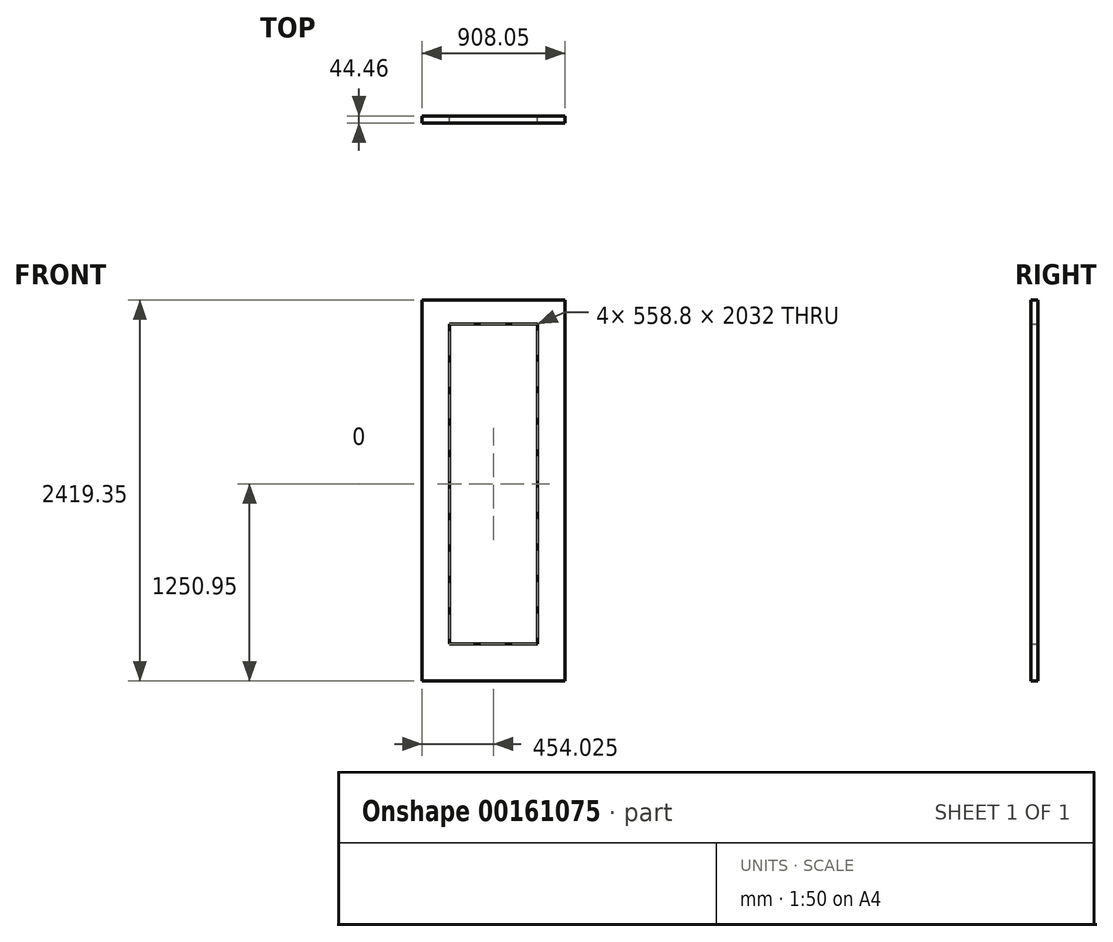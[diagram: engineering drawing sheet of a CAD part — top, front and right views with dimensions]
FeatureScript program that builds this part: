
annotation { "Feature Type Name" : "Feature", "Feature Type Description" : "" }
export const myFeature = defineFeature(function(context is Context, id is Id, definition is map)
    precondition{}
    {
        {
            var Q0;
            Q0=qCreatedBy(makeId("Front.planeOp"),FACE);
            var sketch = newSketch(context, id + "F0", { "sketchPlane" : qUnion([Q0])});
            skLineSegment(sketch, "E0.bottom", {"start": v(0, 0) * mm, "end": v(908.05, 0) * mm});
            skLineSegment(sketch, "E0.top", {"start": v(0, 2419.35) * mm, "end": v(908.05, 2419.35) * mm});
            skLineSegment(sketch, "E0.left", {"start": v(0, 0) * mm, "end": v(0, 2419.35) * mm});
            skLineSegment(sketch, "E0.right", {"start": v(908.05, 0) * mm, "end": v(908.05, 2419.35) * mm});
            skLineSegment(sketch, "E1.bottom", {"start": v(174.62, 2266.95) * mm, "end": v(733.42, 2266.95) * mm});
            skLineSegment(sketch, "E1.top", {"start": v(174.63, 234.95) * mm, "end": v(733.43, 234.95) * mm});
            skLineSegment(sketch, "E1.left", {"start": v(174.62, 2266.95) * mm, "end": v(174.63, 234.95) * mm});
            skLineSegment(sketch, "E1.right", {"start": v(733.42, 2266.95) * mm, "end": v(733.42, 234.95) * mm});
            skSolve(sketch);
        }
        {
            var Q0;
            Q0=qSketchRegion(id+"F0",true);
            extrude(context, id + "F1", {"entities" : qUnion([Q0]), "depth" : 22.22 * mm, "hasSecondDirection" : true, "secondDirectionOppositeDirection" : true, "secondDirectionDepth" : 22.22 * mm});
        }
    });
